# Revit family: RVT_MACOM_CZ71C-AN_AG 12 23 B
name_source: partatom
category: Specialty Equipment
units: mm (PartAtom-declared; Revit-internal decimal feet)

## family parameters
Always vertical = Yes
Cut with Voids When Loaded = No
OmniClass Number = 23.40.40.14.17.11
OmniClass Title = Cookers, Ovens, Stoves
Part Type = Normal
Room Calculation Point = No
Round Connector Dimension = Use Diameter
Shared = No
Work Plane-Based = No

## types (2) — shared parameters
Capacity in Liters = 33,0 L
Capacity in Liters Larger Basket = 18,0 L
Capacity in Liters Smaller Basket = 1,5 L
Default Elevation = 0,000 mm
Depth = 786,000 mm
Description = COZEDOR DE MASSAS MACOM
Gas Connection Height = 71,000 mm
Gas Size = 3/4"
Height = 1162,000 mm
Manufacturer = MACOM
Show Clearances = Yes
Show Larger Basket = Yes
Show Logo = Yes
Show Smaller Basket = Yes
URL = https://www.acosmacom.com.br
Volume = 0,370 mm
Width = 400,000 mm

## per-type parameters (varying)
| type | Gas Consumption GLP | Gas Consumption GN | Gas Input GLP | Gas Input GN | Gas Pressure | Weight |
| CZC1-AG | 0,9 Kg/h | 0 m³/h | 41028 Btu/h |  | 0,03 bar | 56,00 kg |
| CZC1-AN |  | 1 m³/h | 0 Btu/h | 10340 Kcal/h | 0,02 bar | 21,00 kg |

note: column(s) folded — value = type name in every type: Model

## geometry (parser evidence)
native form markers: Sweep x11
no freeform markers — native parametric forms only
